# Revit family: MPR Series Nozzles - Strip
name_source: partatom
category: Conexões de tubo
units: mm (PartAtom-declared; Revit-internal decimal feet)

## family parameters
Com base no plano de trabalho = Sim
Compartilhado = Não
Corte com vazios quando carregada = Não
Cota do conector redondo = Utilizar diâmetro
Número OmniClass = 23.60.30.11.14
Sempre na vertical = Sim
Tipo de parte = Cobertura
Título OmniClass = Pipework Fittings

## types (6) — shared parameters
Aluminum = Aluminum
Angle = 20.00°
Cover = Gray Plastic
DT1 = 0 ft
DT12 = 0 ft
DT13 = 0 ft
DT2 = 0 ft
DT6 = 0 ft
Descrição = Spray Nozzles MPR Series
Elevação-padrão = 4 ft
H2 = 1 ft
Plastic = Plastic Black
RainBird: Product Link = https://store.rainbird.com
Reviw = R00
SupportProjetos: Level of Detail = LOD 300
URL = https://www.rainbird.com
Water = Water

## per-type parameters (varying)
| type | Modelo | Type | Water Visibility (15CST) | Water Visibility (15EST) | Water Visibility (15LCS) | Water Visibility (15RCS) | Water Visibility (SST) |
| 15LCS | 15 LCS | 4 ft | Sim | Sim | Sim | Não | Não |
| 15SST | 15SST | 5 ft | Não | Não | Não | Não | Sim |
| 15RCS | 15 RCS | 3 ft | Não | Não | Não | Sim | Não |
| 9SST | 9 SST | 6 ft | Não | Não | Não | Não | Sim |
| 15EST | 15 EST | 1 ft | Não | Sim | Não | Não | Não |
| 15CST | 15 CST | 2 ft | Sim | Não | Não | Não | Não |
